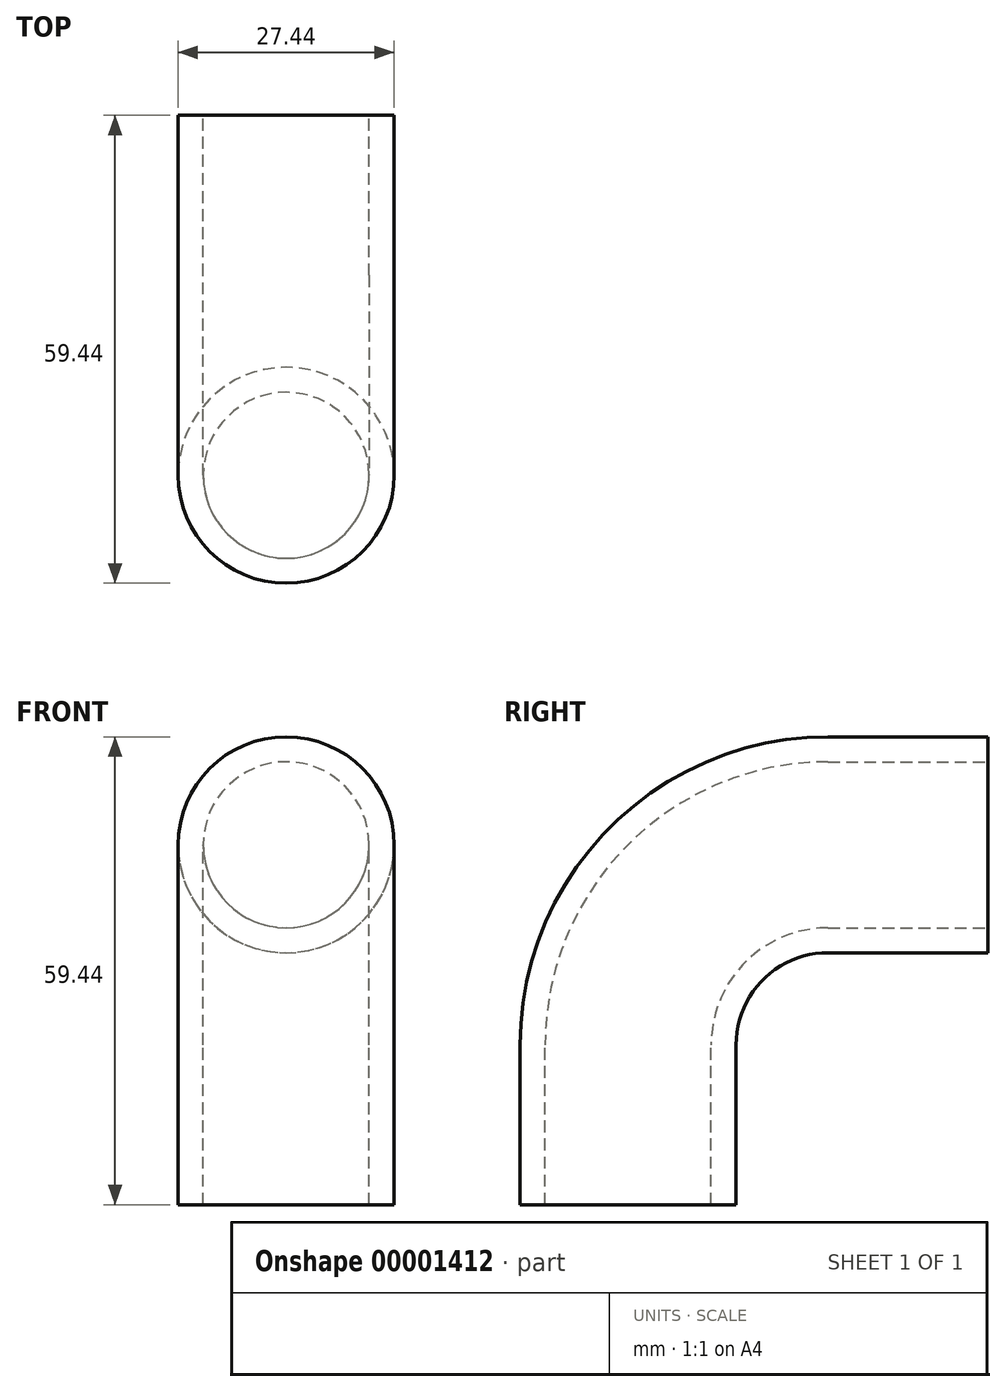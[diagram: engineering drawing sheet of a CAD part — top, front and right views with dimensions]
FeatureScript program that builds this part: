
annotation { "Feature Type Name" : "Feature", "Feature Type Description" : "" }
export const myFeature = defineFeature(function(context is Context, id is Id, definition is map)
    precondition{}
    {
        {
            var Q0;
            Q0=qCreatedBy(makeId("Top.planeOp"),FACE);
            var sketch = newSketch(context, id + "F0", { "sketchPlane" : qUnion([Q0])});
            skCircle(sketch, "E0", {"center": v(0, 0) * mm, "radius": 13.72 * mm});
            skSolve(sketch);
        }
        {
            var Q0;
            Q0=qCreatedBy(makeId("Right.planeOp"),FACE);
            var sketch = newSketch(context, id + "F1", { "sketchPlane" : qUnion([Q0])});
            skLineSegment(sketch, "E1", {"start": v(0, 0) * mm, "end": v(0, 20.32) * mm});
            skLineSegment(sketch, "E2", {"start": v(25.4, 45.72) * mm, "end": v(45.72, 45.72) * mm});
            skPoint(sketch, "E3.visualSharp", {"position": v(0, 45.72) * mm});
            skArc(sketch, "E3.filletArc", {"start": v(25.4, 45.72) * mm, "mid": v(7.44, 38.28) * mm, "end": v(0, 20.32) * mm});
            skSolve(sketch);
        }
        {
            var Q0;
            Q0 = qSketchRegion(id + "F0", true);
            var Q1;
            Q1=sQuery(id+"F1.wireOp",EDGE,"E1");
            var Q2;
            Q2=sQuery(id+"F1.wireOp",EDGE,"E3.filletArc");
            var Q3;
            Q3=sQuery(id+"F1.wireOp",EDGE,"E2");
            sweep(context, id + "F2", {"profiles" : qUnion([Q0]), "path" : qUnion([Q1, Q2, Q3])});
        }
        {
            var Q0;
            Q0=makeQuery(id+"F2.opSweep","CAP_FACE",FACE,{"disambiguationData":[OSD([sQuery(id+"F0.wireOp",EDGE,"E0"),sQuery(id+"F1.wireOp",VERTEX,"E1.start")])],"isStart":true});
            var sketch = newSketch(context, id + "F3", { "sketchPlane" : qUnion([Q0])});
            skCircle(sketch, "E4", {"center": v(0, 0) * mm, "radius": 10.54 * mm});
            skSolve(sketch);
        }
        {
            var Q0;
            Q0 = qSketchRegion(id + "F3", true);
            var Q1;
            Q1=sQuery(id+"F1.wireOp",EDGE,"E2");
            var Q2;
            Q2=sQuery(id+"F1.wireOp",EDGE,"E3.filletArc");
            var Q3;
            Q3=sQuery(id+"F1.wireOp",EDGE,"E1");
            sweep(context, id + "F4", {"operationType" : NewBodyOperationType.REMOVE, "profiles" : qUnion([Q0]), "path" : qUnion([Q1, Q2, Q3])});
        }
    });
